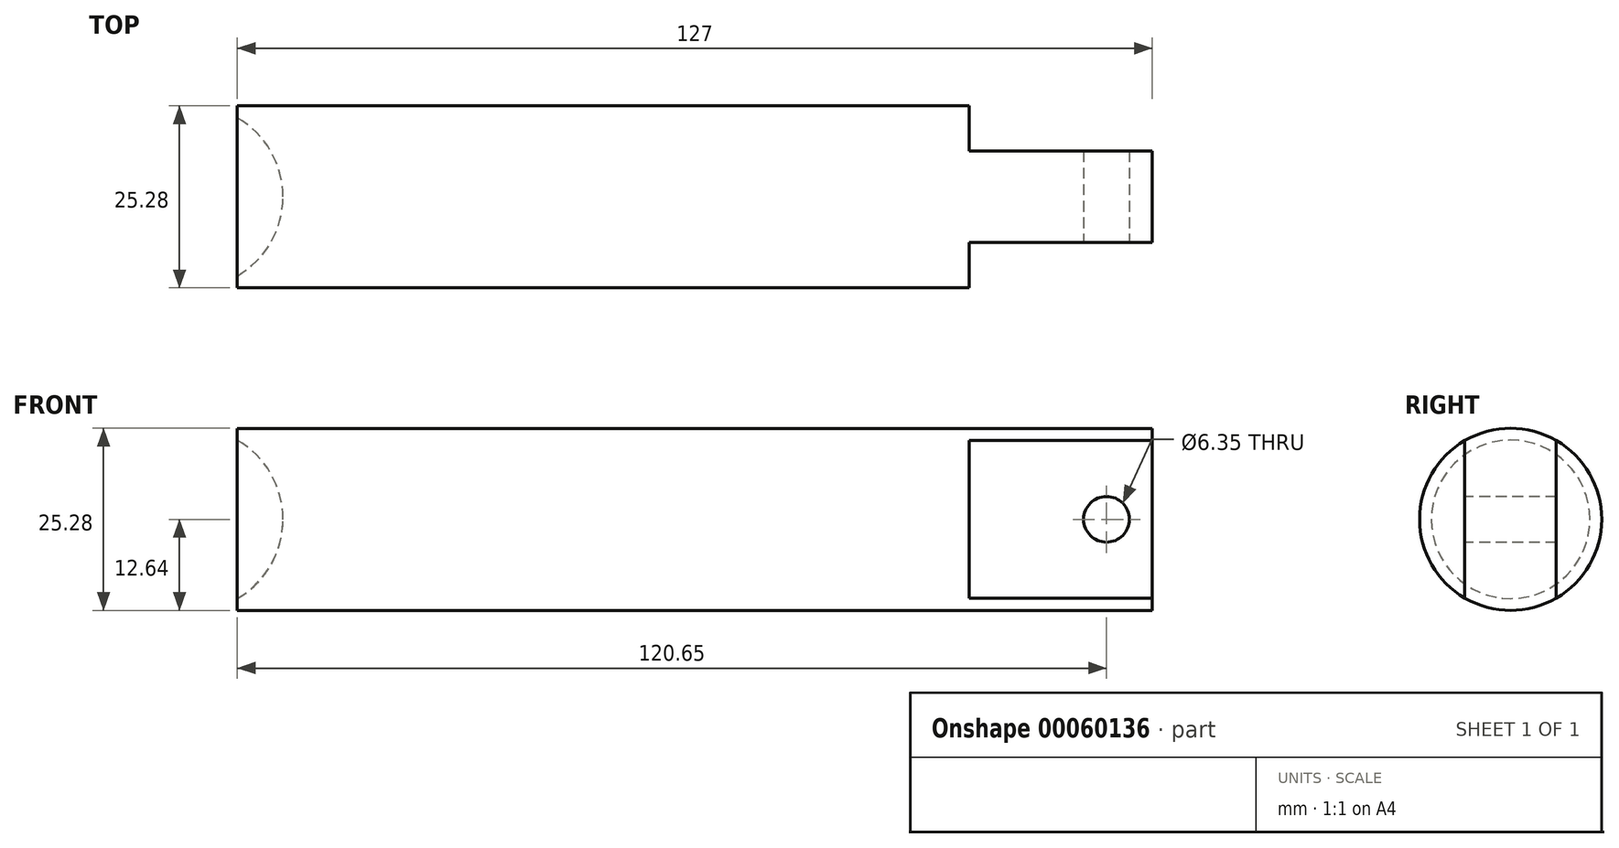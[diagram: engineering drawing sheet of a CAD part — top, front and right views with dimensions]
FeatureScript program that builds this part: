
annotation { "Feature Type Name" : "Feature", "Feature Type Description" : "" }
export const myFeature = defineFeature(function(context is Context, id is Id, definition is map)
    precondition{}
    {
        {
            var Q0;
            Q0=qCreatedBy(makeId("Right.planeOp"),FACE);
            var sketch = newSketch(context, id + "F0", { "sketchPlane" : qUnion([Q0])});
            skCircle(sketch, "E0", {"center": v(0, 0) * mm, "radius": 12.64 * mm});
            skSolve(sketch);
        }
        {
            var Q0;
            Q0 = qSketchRegion(id + "F0", true);
            extrude(context, id + "F1", {"entities" : qUnion([Q0]), "endBound" : BoundingType.SYMMETRIC, "depth" : 127 * mm});
        }
        {
            var Q0;
            Q0=makeQuery(id+"F1.opExtrude","CAP_FACE",FACE,{"disambiguationData":[OSD([sQuery(id+"F0.wireOp",EDGE,"E0")])],"isStart":false});
            var sketch = newSketch(context, id + "F2", { "sketchPlane" : qUnion([Q0])});
            skLineSegment(sketch, "E1.bottom", {"start": v(14.5, -19.26) * mm, "end": v(6.35, -19.26) * mm});
            skLineSegment(sketch, "E1.top", {"start": v(14.5, 19.5) * mm, "end": v(6.35, 19.5) * mm});
            skLineSegment(sketch, "E1.left", {"start": v(14.5, -19.26) * mm, "end": v(14.5, 19.5) * mm});
            skLineSegment(sketch, "E1.right", {"start": v(6.35, -19.26) * mm, "end": v(6.35, 19.5) * mm});
            skLineSegment(sketch, "E2.bottom", {"start": v(-14.98, 20.96) * mm, "end": v(-6.35, 20.96) * mm});
            skLineSegment(sketch, "E2.top", {"start": v(-14.98, -18.77) * mm, "end": v(-6.35, -18.77) * mm});
            skLineSegment(sketch, "E2.left", {"start": v(-14.98, 20.96) * mm, "end": v(-14.98, -18.77) * mm});
            skLineSegment(sketch, "E2.right", {"start": v(-6.35, 20.96) * mm, "end": v(-6.35, -18.77) * mm});
            skSolve(sketch);
        }
        {
            var Q0;
            Q0 = qSketchRegion(id + "F2", true);
            extrude(context, id + "F3", {"entities" : qUnion([Q0]), "operationType" : NewBodyOperationType.REMOVE, "oppositeDirection" : true, "depth" : 25.4 * mm});
        }
        {
            var Q0;
            Q0=makeQuery(id+"F3.boolean.opBoolean","COPY",FACE,{"derivedFrom":makeQuery(id+"F3.opExtrude","SWEPT_FACE",FACE,{"disambiguationData":[OSD([sQuery(id+"F2.wireOp",EDGE,"E2.right")])]})});
            var sketch = newSketch(context, id + "F4", { "sketchPlane" : qUnion([Q0])});
            skCircle(sketch, "E3", {"center": v(57.15, 0) * mm, "radius": 3.18 * mm});
            skSolve(sketch);
        }
        {
            var Q0;
            Q0 = qSketchRegion(id + "F4", true);
            extrude(context, id + "F5", {"entities" : qUnion([Q0]), "operationType" : NewBodyOperationType.REMOVE, "oppositeDirection" : true, "depth" : 25.4 * mm});
        }
        {
            var Q0;
            Q0=qCreatedBy(makeId("Front.planeOp"),FACE);
            var sketch = newSketch(context, id + "F6", { "sketchPlane" : qUnion([Q0])});
            skArc(sketch, "E4", {"start": v(-57.15, 0) * mm, "mid": v(-58.85, 6.35) * mm, "end": v(-63.5, 11) * mm});
            skLineSegment(sketch, "E5", {"start": v(-63.5, 11) * mm, "end": v(-63.5, 0) * mm});
            skLineSegment(sketch, "E6", {"start": v(-63.5, 0) * mm, "end": v(-57.15, 0) * mm});
            skSolve(sketch);
        }
        {
            var Q0;
            Q0 = qSketchRegion(id + "F6", true);
            var Q1;
            Q1=sQuery(id+"F6.wireOp",EDGE,"E6");
            revolve(context, id + "F7", {"operationType" : NewBodyOperationType.REMOVE, "entities" : qUnion([Q0]), "axis" : qUnion([Q1]), "revolveType" : RevolveType.FULL, "oppositeDirection" : true});
        }
    });
